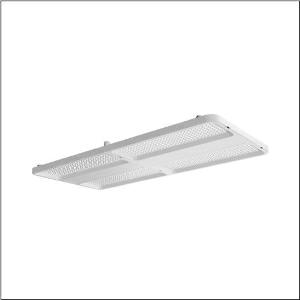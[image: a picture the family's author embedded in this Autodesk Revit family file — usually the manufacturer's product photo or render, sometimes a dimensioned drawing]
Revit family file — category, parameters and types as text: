
# Revit family: highbay_21_maxi_52hn12db4qda02
name_source: partatom
category: Lighting Fixtures
units: mm (PartAtom-declared; Revit-internal decimal feet)

## family parameters
Cut with Voids When Loaded = No
Host = Face
Light Source = No
Part Type = Normal
Room Calculation Point = No
Round Connector Dimension = Use Diameter
Shared = No

## types (1)
- --- (1 x LED, 38000 lm, 198.2 W, 4000K)
    Apparent Load = 198 VA
    CIE Flux Codes = 90 98 100 100 100
    Color Rendering = 80
    Color Temperature = 4000K
    Default Elevation = 1800 mm
    Description = high bay luminaire Highbay 21 maxi; direct symmetric wide distribution, light control with lens of PMMA; UGR ≤ 22 (X = 4H | Y = 8H | S = 0.25H | reflection values 70/50/20); luminous flux: 38.000lm; light colour: 840, colour temperature: 4000K, MacAdam ≤ 3 SDCM (initial), colour rendering: CRI > 80; luminous efficacy: 191,7lm/W; rated service life: 75.000h (L80) at AT= ta max; control: Bluetooth Mesh; for wireless networking: Node luminaire for setting up a local control solution without a higher-level application controller, intelligence completely in the luminaire; no control line such as DALI between the Node multi-sensor luminaires and Nodes is required, wireless integration of other Node luminaires and Node multi-sensor luminaires into the network is possible; number of Node luminaires in the project can be expanded as required, network sizes > 300 Nodes can be realized; can also be connected to lighting or building automation via various gateways upon request; integrated DALI2 ECG provides luminaire data (according to IEC62386, Part 251), energy data (Part 252), and monitoring and analytics data (Part 253) to higher-level systems for further processing; luminaire connection: terminal, 5-pole, max. 2.5mm² (cable entry for one cable, Ø 8.5..16mm); mains connection: 230..240V, AC 50/60Hz; connected load: 198,2W; protection rating (complete): IP66; insulation class (complete): insulation class I (protective earthing); protection symbol: D; impact resistance: IK08; certification: CE, UKCA; internal wiring halogen-free; luminaire LABS conformity tested according to VDMA 24364:2018-05; Suitable for use in the food industry according to the specifications of IFS-Food, HACCP and/or BRC; housing frame of high-performance plastic PA6, matt traffic white (RAL 9016); cover of PMMA; dimension (LxWxH): 946 x 442 x 72mm; permissible operating ambient temperature: -20..+40°C (reducing of maximum allowable ambient temperature of 5°C with ceiling mounting); packaging unit: 1 piece; (delivery without accessories; please order mounting accessories separately)
    Height = 72 mm  [stored 0.23622 ft]
    Lamp = 1 x LED
    Lamp Light Flux = 38000 lm
    Lamp Power = 198.2 W
    Lamp count = 1
    Length = 946 mm
    Luminous efficacy = 192 lm/W
    Manufacturer = Siteco
    ModVariant = No
    Model = 52HN12DB4QDA02
    Mounting Place = Ceiling
    Mounting Type = Pendant
    Number of Poles = 1
    OnlyDefault = Yes
    Power Factor = 1
    Product Name = Highbay 21 maxi
    Product group = high bay luminaire
    ProductGroupID = 902
    Protection Class = Protection class I
    Protection Degree = IP 66
    RLX_Detail_Level = 1
    RLX_Emergency_Light_Flux = 0 lm
    RLX_Emergency_Type = 0
    RLX_Emergency_Type_DB = No
    RlxData = <blob elided: 128889 chars, md5=c4c1d5e1>
    Socket = socket
    Standby Power = 0 W
    System Light Flux = 38001 lm
    System Power = 198 W
    Type Comments = factory setting: luminous flux: 100 % | dim-lin: 254 | 918 mA
    Type Image = l_1363244.jpg
    URL = http://relux.com
    VarID = @adj_014003
    Voltage = 0 V
    Weight = 0.00 kg
    Width = 442 mm

note: [stored X ft] marks values corroborated as IEEE doubles in the binary element streams (Revit-internal decimal feet)

## geometry (parser evidence)
native form markers: Blend x4, Sweep x9
no freeform markers — native parametric forms only
